# Revit family: Suszarka_do_rak_ORKAN 2000W
name_source: partatom
category: Electrical Equipment
units: mm (PartAtom-declared; Revit-internal decimal feet)

## family parameters
Always vertical = Yes
Cut with Voids When Loaded = No
Host = Wall
Part Type = Panelboard
Room Calculation Point = No
Round Connector Dimension = Use Diameter
Shared = No

## types (1)
- Type 1
    Color / Kolor = White / Biały
    Depth / Glebokosc = 130 mm  [stored 0.426509 ft]
    Description = SSuszarka do rąk 2000 W ORKAN wykonana jest z bardzo mocnego, białego plastiku ABS. Pokryta jest antybakteryjną powłoką, zapewniającą użytkownikom najwyższy stopień higieny. Jak wszystkie suszarki strumieniowe różni się od tradycyjnych sposobem suszenia dłoni. Mokre ręce umieszcza się w przestrzeni przypominającej kieszeń (stąd suszarki określa się również kieszeniowymi), co automatycznie uruchamia suszarkę do działania. Z wąskich szczelin wylatuje z dużą prędkością powietrze, które w krótkim czasie ściąga wodę z dłoni. ORKAN jest więc wysokiej klasy urządzeniem, które równocześnie zapewnia skuteczność działania, jak i niskie koszty eksploatacji. Idealnie pasuje do toalet o średnim i dużym natężeniu ruchu.
    Height / Wysokosc = 530 mm  [stored 1.73885 ft]
    Manufacturer = FANECO.com
    Manufacturer code / Kod producenta = 5901764296430
    Material finish / Wykonczenie = Plastik ABS
    Model = ORKAN
    Product code / Kod produktu = DA2000PRW
    Type Comments = Suszarka do rąk 2000 W ORKAN
    URL = https://faneco.com
    Wattage = 2000
    Weight / Waga = 9 kg
    Width / Szerokosc = 295 mm  [stored 0.967848 ft]

note: [stored X ft] marks values corroborated as IEEE doubles in the binary element streams (Revit-internal decimal feet)

## geometry (parser evidence)
native form markers: Sweep x9
no freeform markers — native parametric forms only
